# Revit family: P6080
name_source: partatom
category: Plumbing Fixtures
revit_build: Autodesk Revit 2018 (Build: 20170223_1515(x64)
units: mm (PartAtom-declared; Revit-internal decimal feet)

## family parameters
Cut with Voids When Loaded = No
Host = Face
Part Type = Normal
Room Calculation Point = No
Round Connector Dimension = Use Diameter
Shared = No

## types (20) — shared parameters
Default Elevation = 48.00"
Description = 10" WIDE, 8" INTERNAL WIDTH, STAINLESS STEEL BODY AND GRATE SYSTEM
Manufacturer = MIFAB
Material = Paint - Sherwin Williams Paint - #952C2A - Bellwood Red
URL = WWW.MIFAB.COM

## per-type parameters (varying)
| type | C1_(Shallow invert) | LENGTH |
| P6081-PB | 6.00" | 78.74" |
| P6081N-PB | 6.78" | 78.74" |
| P6081N-PB-B04 | 6.78" | 78.74" |
| P6081N-PB-B06 | 6.78" | 78.74" |
| P6081N-PB-B08 | 6.78" | 78.74" |
| P6081N-PB-1M | 6.78" | 39.37" |
| P6082-PB | 6.78" | 78.74" |
| P6083-PB | 7.56" | 78.74" |
| P6083N-PB | 8.34" | 78.74" |
| P6083N-PB-B04 | 8.34" | 78.74" |
| P6083N-PB-B06 | 8.34" | 78.74" |
| P6083N-PB-B08 | 8.34" | 78.74" |
| P6083N-PB-1M | 8.34" | 39.37" |
| P6084-PB | 8.34" | 78.74" |
| P6085-PB | 9.12" | 78.74" |
| P6085N-PB | 9.90" | 78.74" |
| P6085N-PB-B04 | 9.90" | 78.74" |
| P6085N-PB-B06 | 9.90" | 78.74" |
| P6085N-PB-B08 | 9.90" | 78.74" |
| P6085N-PB-1M | 9.90" | 39.37" |

note: column(s) folded — value = type name in every type: Model

## geometry (parser evidence)
native form markers: Blend x2, Sweep x2
no freeform markers — native parametric forms only
